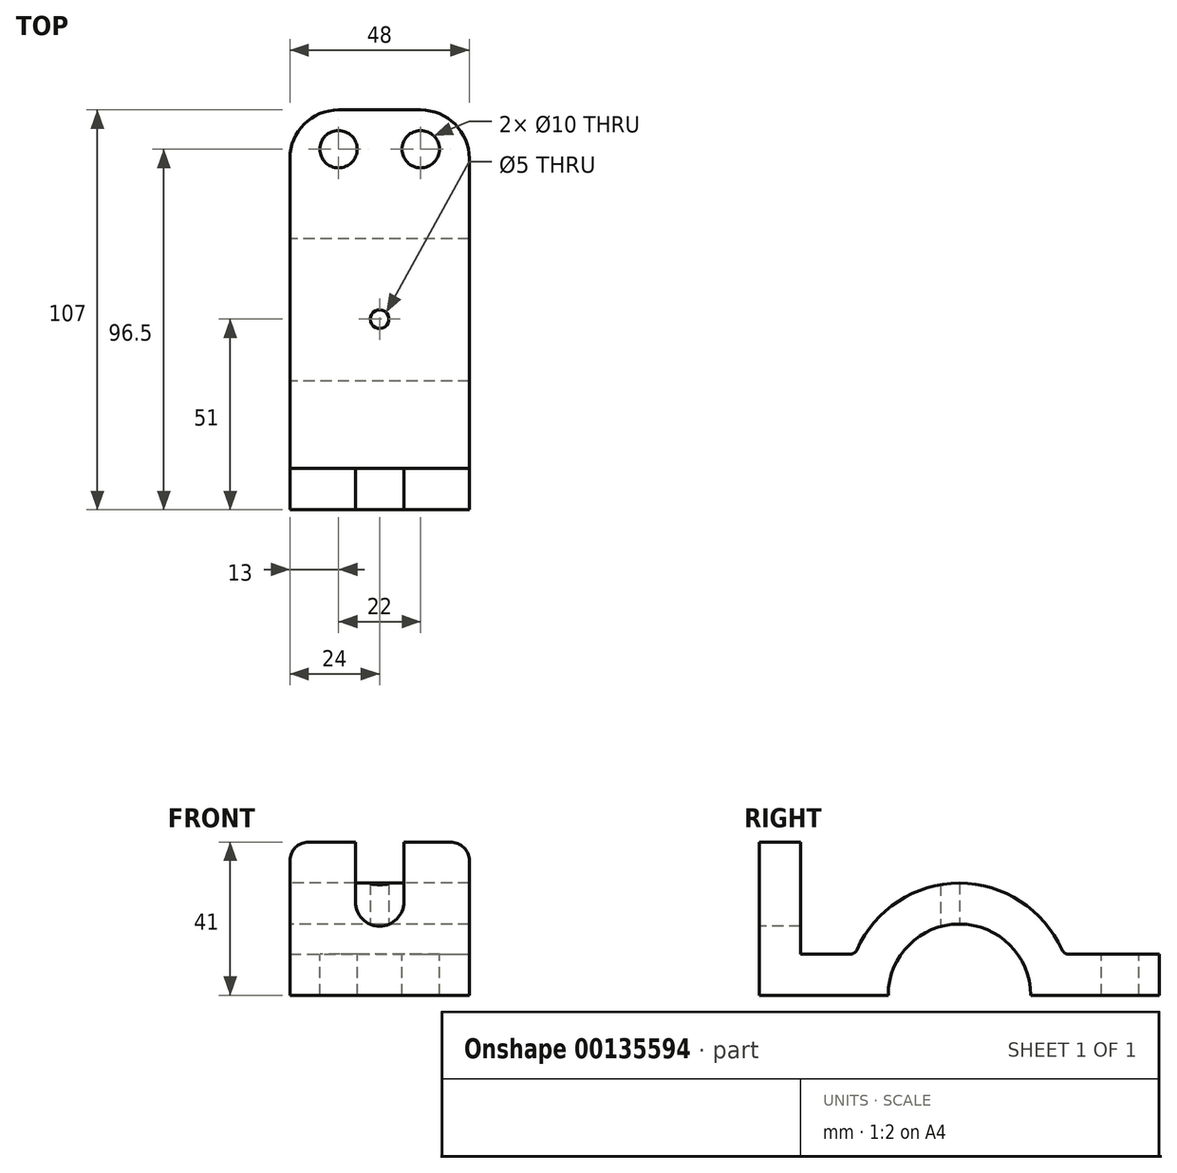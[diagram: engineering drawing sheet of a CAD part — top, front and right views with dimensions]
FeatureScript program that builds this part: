
annotation { "Feature Type Name" : "Feature", "Feature Type Description" : "" }
export const myFeature = defineFeature(function(context is Context, id is Id, definition is map)
    precondition{}
    {
        {
            var Q0;
            Q0=qCreatedBy(makeId("Right.planeOp"),FACE);
            var sketch = newSketch(context, id + "F0", { "sketchPlane" : qUnion([Q0])});
            skLineSegment(sketch, "E0", {"start": v(0, 0) * mm, "end": v(34.45, 0) * mm});
            skLineSegment(sketch, "E1", {"start": v(107, 0) * mm, "end": v(107, 11) * mm});
            skLineSegment(sketch, "E2", {"start": v(0, 0) * mm, "end": v(0, 41) * mm});
            skLineSegment(sketch, "E3", {"start": v(0, 41) * mm, "end": v(11, 41) * mm});
            skLineSegment(sketch, "E4", {"start": v(11, 41) * mm, "end": v(11, 11) * mm});
            skPoint(sketch, "E5", {"position": v(53.5, 0) * mm});
            skArc(sketch, "E6", {"start": v(72.55, 0) * mm, "mid": v(53.5, 19.05) * mm, "end": v(34.45, 0) * mm});
            skArc(sketch, "E7", {"start": v(81.41, 11) * mm, "mid": v(53.5, 30) * mm, "end": v(25.59, 11) * mm});
            skLineSegment(sketch, "E8", {"start": v(11, 11) * mm, "end": v(25.59, 11) * mm});
            skLineSegment(sketch, "E9", {"start": v(107, 11) * mm, "end": v(81.41, 11) * mm});
            skLineSegment(sketch, "E10.trimOffspring", {"start": v(72.55, 0) * mm, "end": v(107, 0) * mm});
            skSolve(sketch);
        }
        {
            var Q0;
            Q0 = qSketchRegion(id + "F0", true);
            extrude(context, id + "F1", {"entities" : qUnion([Q0]), "endBound" : BoundingType.SYMMETRIC, "depth" : 48 * mm});
        }
        {
            var Q0;
            Q0=makeQuery(id+"F1.opExtrude","CAP_EDGE",EDGE,{"disambiguationData":[OSD([sQuery(id+"F0.wireOp",EDGE,"E1")])],"isStart":false});
            var Q1;
            Q1=makeQuery(id+"F1.opExtrude","CAP_EDGE",EDGE,{"disambiguationData":[OSD([sQuery(id+"F0.wireOp",EDGE,"E1")])],"isStart":true});
            fillet(context, id + "F2", {"entities" : qUnion([Q0, Q1]), "radius" : 13 * mm, "tangentPropagation" : true, "allowEdgeOverflow" : false});
        }
        {
            var Q0;
            Q0=makeQuery(id+"F1.opExtrude","CAP_EDGE",EDGE,{"disambiguationData":[OSD([sQuery(id+"F0.wireOp",EDGE,"E3")])],"isStart":true});
            var Q1;
            Q1=makeQuery(id+"F1.opExtrude","CAP_EDGE",EDGE,{"disambiguationData":[OSD([sQuery(id+"F0.wireOp",EDGE,"E3")])],"isStart":false});
            fillet(context, id + "F3", {"entities" : qUnion([Q0, Q1]), "radius" : 5 * mm, "tangentPropagation" : true, "allowEdgeOverflow" : false});
        }
        {
            var Q0;
            Q0=makeQuery(id+"F1.opExtrude","SWEPT_FACE",FACE,{"disambiguationData":[OSD([sQuery(id+"F0.wireOp",EDGE,"E2")])]});
            var sketch = newSketch(context, id + "F4", { "sketchPlane" : qUnion([Q0])});
            skArc(sketch, "E11", {"start": v(-6.5, 25) * mm, "mid": v(0, 18.5) * mm, "end": v(6.5, 25) * mm});
            skLineSegment(sketch, "E12", {"start": v(-6.5, 25) * mm, "end": v(-6.5, 41) * mm});
            skLineSegment(sketch, "E13", {"start": v(6.5, 25) * mm, "end": v(6.5, 41) * mm});
            skLineSegment(sketch, "E14", {"start": v(6.5, 41) * mm, "end": v(-6.5, 41) * mm});
            skSolve(sketch);
        }
        {
            var Q0;
            Q0 = qSketchRegion(id + "F4", true);
            extrude(context, id + "F5", {"entities" : qUnion([Q0]), "operationType" : NewBodyOperationType.REMOVE, "endBound" : BoundingType.UP_TO_NEXT, "oppositeDirection" : true, "depth" : 25 * mm});
        }
        {
            var Q0;
            Q0=qCreatedBy(makeId("Top.planeOp"),FACE);
            var sketch = newSketch(context, id + "F6", { "sketchPlane" : qUnion([Q0])});
            skCircle(sketch, "E15", {"center": v(0, 51) * mm, "radius": 2.5 * mm});
            skSolve(sketch);
        }
        {
            var Q0;
            Q0 = qSketchRegion(id + "F6", true);
            extrude(context, id + "F7", {"entities" : qUnion([Q0]), "operationType" : NewBodyOperationType.REMOVE, "endBound" : BoundingType.THROUGH_ALL, "depth" : 25 * mm});
        }
        {
            var Q0;
            Q0=makeQuery(id+"F1.opExtrude","SWEPT_FACE",FACE,{"disambiguationData":[OSD([sQuery(id+"F0.wireOp",EDGE,"E9")])]});
            var sketch = newSketch(context, id + "F8", { "sketchPlane" : qUnion([Q0])});
            skCircle(sketch, "E16", {"center": v(-11, 96.5) * mm, "radius": 5 * mm});
            skCircle(sketch, "E17.MirrorC", {"center": v(11, 96.5) * mm, "radius": 5 * mm});
            skLineSegment(sketch, "E18", {"start": v(-11, 96.5) * mm, "end": v(11, 96.5) * mm, "construction": true});
            skSolve(sketch);
        }
        {
            var Q0;
            Q0 = qSketchRegion(id + "F8", true);
            extrude(context, id + "F9", {"entities" : qUnion([Q0]), "operationType" : NewBodyOperationType.REMOVE, "endBound" : BoundingType.THROUGH_ALL, "oppositeDirection" : true, "depth" : 25 * mm});
        }
        {
            var Q0;
            Q0=makeQuery(id+"F1.opExtrude","SWEPT_EDGE",EDGE,{"disambiguationData":[OSD([sQuery(id+"F0.wireOp",EDGE,"E7"),sQuery(id+"F0.wireOp",EDGE,"E8")])]});
            var Q1;
            Q1=makeQuery(id+"F1.opExtrude","SWEPT_EDGE",EDGE,{"disambiguationData":[OSD([sQuery(id+"F0.wireOp",EDGE,"E7"),sQuery(id+"F0.wireOp",EDGE,"E9")])]});
            fillet(context, id + "F10", {"entities" : qUnion([Q0, Q1]), "radius" : 2 * mm, "tangentPropagation" : true, "allowEdgeOverflow" : false});
        }
    });
